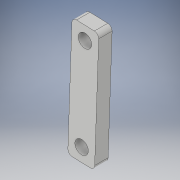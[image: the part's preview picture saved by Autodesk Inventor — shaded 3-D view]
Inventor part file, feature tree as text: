
AUTODESK INVENTOR PART (.ipt)
format: ipt  version: 2019 (Build 230136000, 136)  size: 114,688 bytes
history: native  units: in
note: dims shown in document units (in); Inventor stores cm internally (conversion verified against a paired STEP export)
features: other x4, reference x2, extrude x1, sketch x1
ambient origin geometry x8: Origin, YZ Plane, XZ Plane, XY Plane, X Axis, Y Axis, Z Axis, Center Point
bodies: Solid1 (feature_tree)
feature tree (8):
  extrude  "Extrusion1"  Depth=0.1181in
  sketch  "Sketch1"  dims[d0=0.236in d1=0.118in d2=0.118in d3=0.118in d4=0.118in d6=0.118in d7=0.118in d8=0.0394in d9=0.1181in d10=0.0in]
  reference  "Reference1"
  reference  "Reference2"
  other  "<userpath>\Documents\Inventor\Glyptodon Head\Head Assemble.iam"
  other  "Head Assemble.iam"
  other  "Mouth:1"
  other  "SyringeHeadLeverAttachmentNew:1"
